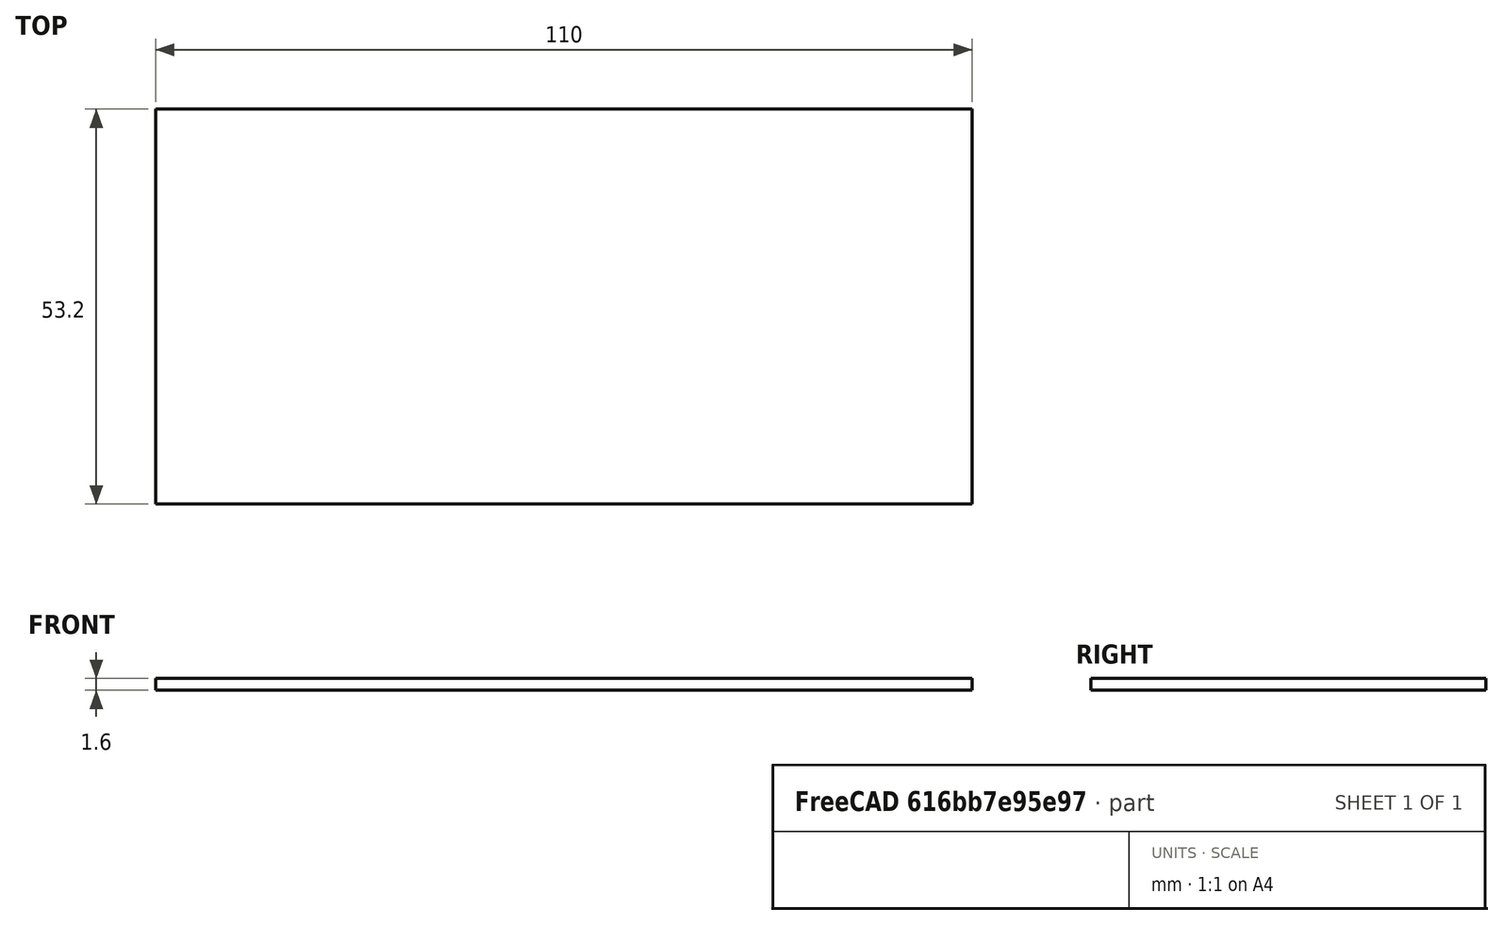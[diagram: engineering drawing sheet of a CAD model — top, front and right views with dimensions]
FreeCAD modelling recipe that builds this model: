
FCSTD DOCUMENT  (FreeCAD 0.19R24276 (Git))
Label: pir-baffel-side
License: All rights reserved
LicenseURL: http://en.wikipedia.org/wiki/All_rights_reserved
objects: Sketcher::SketchObject×1, PartDesign::Pad×1, PartDesign::CoordinateSystem×1, PartDesign::Body×1
note: 5 computed .brp shape members not serialized (recipe doc carries the construction recipe); baked Part::Feature solids carry a one-line shape summary decoded from their .brp

FEATURE [Sketcher::SketchObject] Sketch
  FullyConstrained = true
  MapMode = 5
  Support = -> [XY_Plane]
  sketch-geometry (4):
    g0: LineSegment StartX=-55 StartY=26.6 StartZ=0 EndX=55 EndY=26.6 EndZ=0
    g1: LineSegment StartX=55 StartY=26.6 StartZ=0 EndX=55 EndY=-26.6 EndZ=0
    g2: LineSegment StartX=55 StartY=-26.6 StartZ=0 EndX=-55 EndY=-26.6 EndZ=0
    g3: LineSegment StartX=-55 StartY=-26.6 StartZ=0 EndX=-55 EndY=26.6 EndZ=0
  constraints (10):
    c: Coincident(g0,g1)
    c: Coincident(g1,g2)
    c: Coincident(g2,g3)
    c: Coincident(g3,g0)
    c: Horizontal(g2)
    c: Vertical(g1)
    c: DistanceY(g3,g3) = 53.2
    c: DistanceX(g0,g0) = 110
    c: Symmetric(g0,g0,g-2)
    c: Symmetric(g0,g2,g-1)
FEATURE [PartDesign::Pad] Pad  label="Side"
  Direction = (1,1,1)
  Length = 1.6
  Length2 = 100
  Profile = -> Sketch
  Type = 0
FEATURE [PartDesign::CoordinateSystem] LCS_side
  AttacherType = Attacher::AttachEngine3D
  MapMode = 45
  Placement = pos=(7e-16,-0.776642,1.57664) rot=(0.001211,-0.001211,0.999999;1.5708rad)
  Support = -> [Pad]
FEATURE [PartDesign::Body] Body
  Group = -> [Sketch,Pad,LCS_side]
  Origin = -> Origin
  Tip = -> Pad
